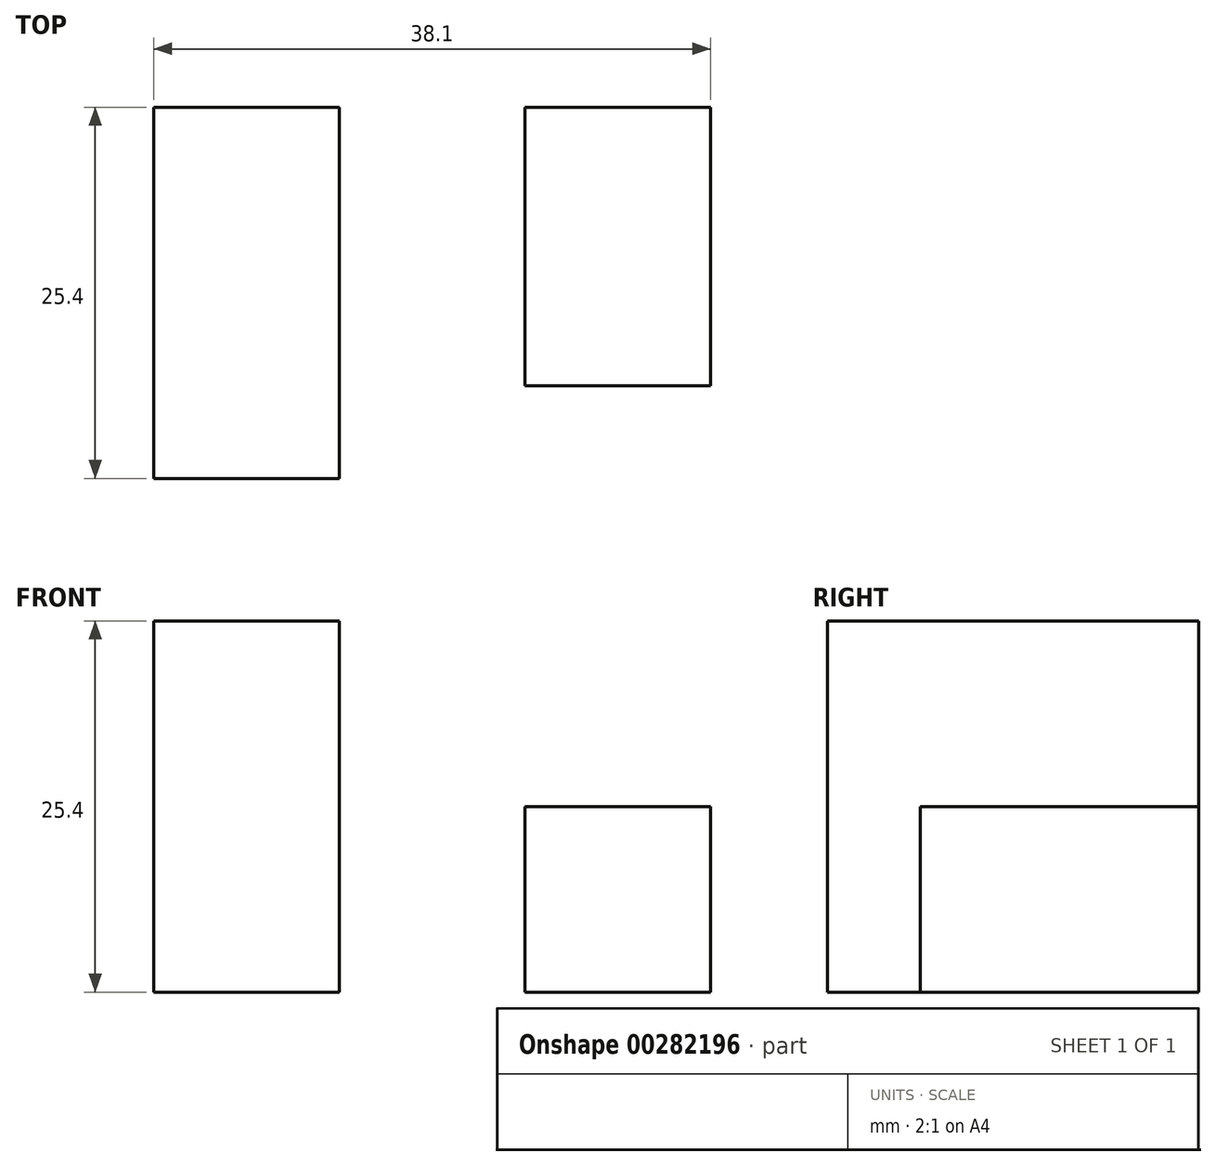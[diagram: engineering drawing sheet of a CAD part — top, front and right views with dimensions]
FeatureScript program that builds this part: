
annotation { "Feature Type Name" : "Feature", "Feature Type Description" : "" }
export const myFeature = defineFeature(function(context is Context, id is Id, definition is map)
    precondition{}
    {
        {
            var Q0;
            Q0=qCreatedBy(makeId("Front.planeOp"),FACE);
            var sketch = newSketch(context, id + "F0", { "sketchPlane" : qUnion([Q0])});
            skLineSegment(sketch, "E0.bottom", {"start": v(-19.05, 25.4) * mm, "end": v(19.05, 25.4) * mm});
            skLineSegment(sketch, "E0.top", {"start": v(-19.05, 0) * mm, "end": v(19.05, 0) * mm});
            skLineSegment(sketch, "E0.left", {"start": v(-19.05, 25.4) * mm, "end": v(-19.05, 0) * mm});
            skLineSegment(sketch, "E0.right", {"start": v(19.05, 25.4) * mm, "end": v(19.05, 0) * mm});
            skLineSegment(sketch, "E1", {"start": v(19.05, 12.7) * mm, "end": v(6.35, 12.7) * mm});
            skLineSegment(sketch, "E2", {"start": v(6.35, 12.7) * mm, "end": v(6.35, 0) * mm});
            skLineSegment(sketch, "E3", {"start": v(-19.05, 25.4) * mm, "end": v(-6.35, 25.4) * mm});
            skLineSegment(sketch, "E4", {"start": v(-6.35, 25.4) * mm, "end": v(-6.35, 0) * mm});
            skLineSegment(sketch, "E5", {"start": v(-6.35, 0) * mm, "end": v(-19.05, 0) * mm});
            skSolve(sketch);
        }
        {
            var Q0;
            {var subQ4=sQuery(id+"F0.wireOp",EDGE,"E1");Q0=makeQuery(id+"F0.imprint","IMPRINT",FACE,{"disambiguationData":[TD([[makeQuery(id+"F0.imprint","IMPRINT",EDGE,{"derivedFrom":subQ4}),1.0]])]});}
            var Q1;
            {var subQ1=sQuery(id+"F0.wireOp",EDGE,"E0.bottom");Q1=makeQuery(id+"F0.imprint","IMPRINT",FACE,{"disambiguationData":[TD([[makeQuery(id+"F0.imprint","IMPRINT",EDGE,{"derivedFrom":subQ1}),-1.0]])]});}
            var Q2;
            Q2=makeQuery(id+"F0.imprint","IMPRINT",FACE,{"disambiguationData":[TD([[makeQuery(id+"F0.imprint","IMPRINT",EDGE,{"derivedFrom":sQuery(id+"F0.wireOp",EDGE,"E0.left")}),1.0]])]});
            extrude(context, id + "F1", {"entities" : qUnion([Q0, Q1, Q2]), "oppositeDirection" : true, "depth" : 12.7 * mm});
        }
        {
            var Q0;
            Q0=makeQuery(id+"F0.imprint","IMPRINT",FACE,{"disambiguationData":[TD([[makeQuery(id+"F0.imprint","IMPRINT",EDGE,{"derivedFrom":sQuery(id+"F0.wireOp",EDGE,"E0.left")}),1.0]])]});
            extrude(context, id + "F2", {"entities" : qUnion([Q0]), "operationType" : NewBodyOperationType.ADD, "depth" : 12.7 * mm});
        }
        {
            var Q0;
            {var subQ4=sQuery(id+"F0.wireOp",EDGE,"E1");Q0=makeQuery(id+"F0.imprint","IMPRINT",FACE,{"disambiguationData":[TD([[makeQuery(id+"F0.imprint","IMPRINT",EDGE,{"derivedFrom":subQ4}),1.0]])]});}
            extrude(context, id + "F3", {"entities" : qUnion([Q0]), "operationType" : NewBodyOperationType.ADD, "depth" : 6.35 * mm});
        }
    });
